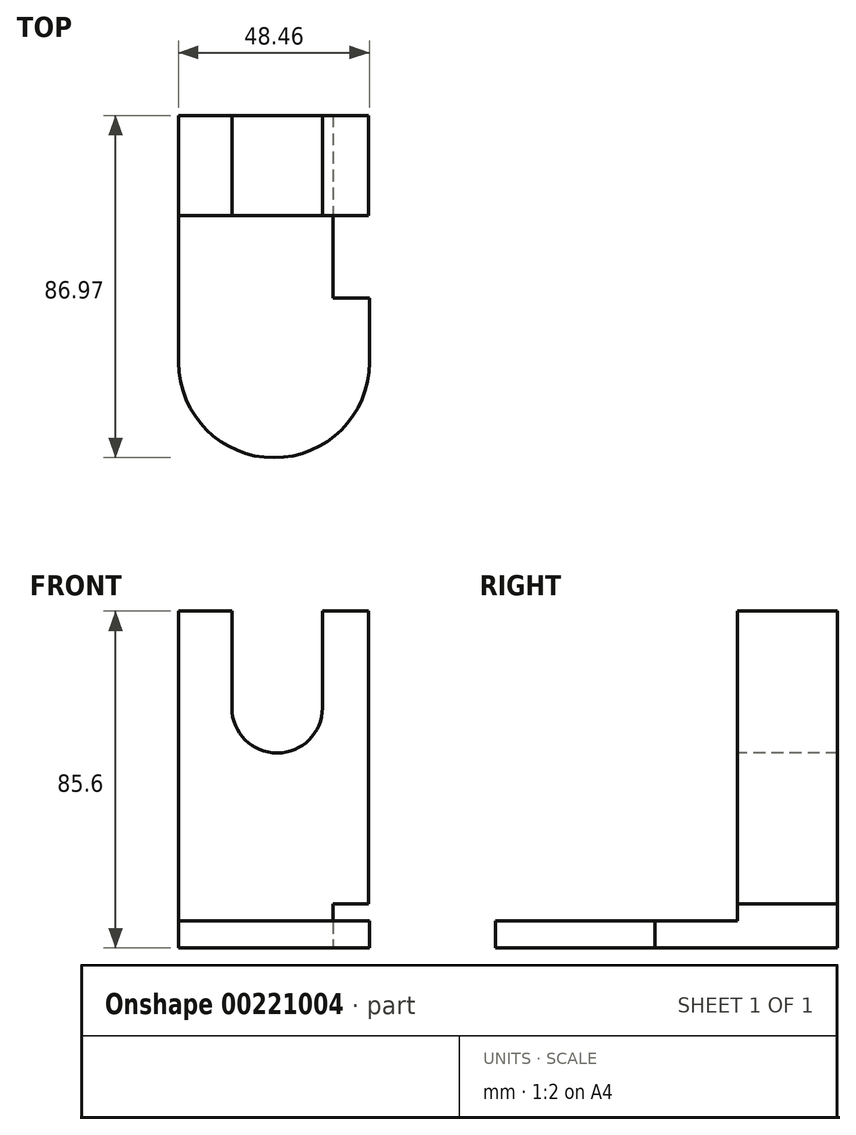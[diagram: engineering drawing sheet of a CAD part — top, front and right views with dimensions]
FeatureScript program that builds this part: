
annotation { "Feature Type Name" : "Feature", "Feature Type Description" : "" }
export const myFeature = defineFeature(function(context is Context, id is Id, definition is map)
    precondition{}
    {
        {
            var Q0;
            Q0=qCreatedBy(makeId("Front.planeOp"),FACE);
            var sketch = newSketch(context, id + "F0", { "sketchPlane" : qUnion([Q0])});
            skLineSegment(sketch, "E0.bottom", {"start": v(-21.81, 38.95) * mm, "end": v(26.4, 38.95) * mm});
            skLineSegment(sketch, "E0.top", {"start": v(-21.81, -46.65) * mm, "end": v(26.4, -46.65) * mm});
            skLineSegment(sketch, "E0.left", {"start": v(-21.81, 38.95) * mm, "end": v(-21.81, -46.65) * mm});
            skLineSegment(sketch, "E0.right", {"start": v(26.4, 38.95) * mm, "end": v(26.4, -46.65) * mm});
            skSolve(sketch);
        }
        {
            var Q0;
            Q0=makeQuery(id+"F0.imprint","IMPRINT",FACE,{"disambiguationData":[TD([[makeQuery(id+"F0.imprint","IMPRINT",EDGE,{"derivedFrom":sQuery(id+"F0.wireOp",EDGE,"E0.bottom")}),-1.0]])]});
            extrude(context, id + "F1", {"entities" : qUnion([Q0]), "depth" : 25.4 * mm});
        }
        {
            var Q0;
            Q0=makeQuery(id+"F1.opExtrude","CAP_FACE",FACE,{"disambiguationData":[OSD([sQuery(id+"F0.wireOp",EDGE,"E0.bottom"),sQuery(id+"F0.wireOp",EDGE,"E0.top"),sQuery(id+"F0.wireOp",EDGE,"E0.left"),sQuery(id+"F0.wireOp",EDGE,"E0.right")])],"isStart":false});
            var sketch = newSketch(context, id + "F2", { "sketchPlane" : qUnion([Q0])});
            skLineSegment(sketch, "E1", {"start": v(-8.28, 38.95) * mm, "end": v(-8.28, 14.42) * mm});
            skLineSegment(sketch, "E2", {"start": v(14.75, 38.95) * mm, "end": v(14.75, 14.42) * mm});
            skArc(sketch, "E3", {"start": v(-8.28, 14.42) * mm, "mid": v(3.23, 2.9) * mm, "end": v(14.75, 14.42) * mm});
            skLineSegment(sketch, "E4", {"start": v(-8.28, 38.95) * mm, "end": v(14.75, 38.95) * mm});
            skSolve(sketch);
        }
        {
            var Q0;
            Q0 = qSketchRegion(id + "F2", true);
            extrude(context, id + "F3", {"entities" : qUnion([Q0]), "operationType" : NewBodyOperationType.REMOVE, "oppositeDirection" : true, "depth" : 25.4 * mm});
        }
        {
            var Q0;
            Q0=makeQuery(id+"F1.opExtrude","CAP_FACE",FACE,{"disambiguationData":[OSD([sQuery(id+"F0.wireOp",EDGE,"E0.bottom"),sQuery(id+"F0.wireOp",EDGE,"E0.top"),sQuery(id+"F0.wireOp",EDGE,"E0.left"),sQuery(id+"F0.wireOp",EDGE,"E0.right")])],"isStart":false});
            var sketch = newSketch(context, id + "F4", { "sketchPlane" : qUnion([Q0])});
            skLineSegment(sketch, "E5.bottom", {"start": v(27.72, -35.4) * mm, "end": v(17.38, -35.4) * mm});
            skLineSegment(sketch, "E5.top", {"start": v(27.72, -46.65) * mm, "end": v(17.38, -46.65) * mm});
            skLineSegment(sketch, "E5.left", {"start": v(27.72, -35.4) * mm, "end": v(27.72, -46.65) * mm});
            skLineSegment(sketch, "E5.right", {"start": v(17.38, -35.4) * mm, "end": v(17.38, -46.65) * mm});
            skLineSegment(sketch, "E6.bottom", {"start": v(27.72, -35.4) * mm, "end": v(29.95, -35.4) * mm});
            skLineSegment(sketch, "E6.top", {"start": v(27.72, -46.65) * mm, "end": v(29.95, -46.65) * mm});
            skLineSegment(sketch, "E6.right", {"start": v(29.95, -35.4) * mm, "end": v(29.95, -46.65) * mm});
            skSolve(sketch);
        }
        {
            var Q0;
            Q0 = qSketchRegion(id + "F4", true);
            extrude(context, id + "F5", {"entities" : qUnion([Q0]), "operationType" : NewBodyOperationType.REMOVE, "oppositeDirection" : true, "depth" : 25.4 * mm});
        }
        {
            var Q0;
            Q0=makeQuery(id+"F1.opExtrude","SWEPT_FACE",FACE,{"disambiguationData":[OSD([sQuery(id+"F0.wireOp",EDGE,"E0.top")])]});
            var sketch = newSketch(context, id + "F6", { "sketchPlane" : qUnion([Q0])});
            skLineSegment(sketch, "E7", {"start": v(-21.81, 25.4) * mm, "end": v(-21.81, 62.74) * mm});
            skLineSegment(sketch, "E8", {"start": v(17.38, 25.4) * mm, "end": v(17.38, 46.43) * mm});
            skLineSegment(sketch, "E9", {"start": v(17.38, 46.43) * mm, "end": v(26.65, 46.43) * mm});
            skLineSegment(sketch, "E10", {"start": v(26.65, 46.43) * mm, "end": v(26.65, 62.74) * mm});
            skArc(sketch, "E11", {"start": v(26.65, 62.74) * mm, "mid": v(2.42, 86.97) * mm, "end": v(-21.81, 62.74) * mm});
            skSolve(sketch);
        }
        {
            var Q0;
            Q0=makeQuery(id+"F6.imprint","IMPRINT",FACE,{"disambiguationData":[TD([[makeQuery(id+"F6.imprint","IMPRINT",EDGE,{"derivedFrom":sQuery(id+"F6.wireOp",EDGE,"E7")}),-1.0]])]});
            extrude(context, id + "F7", {"entities" : qUnion([Q0]), "operationType" : NewBodyOperationType.ADD, "oppositeDirection" : true, "depth" : 6.86 * mm});
        }
    });
